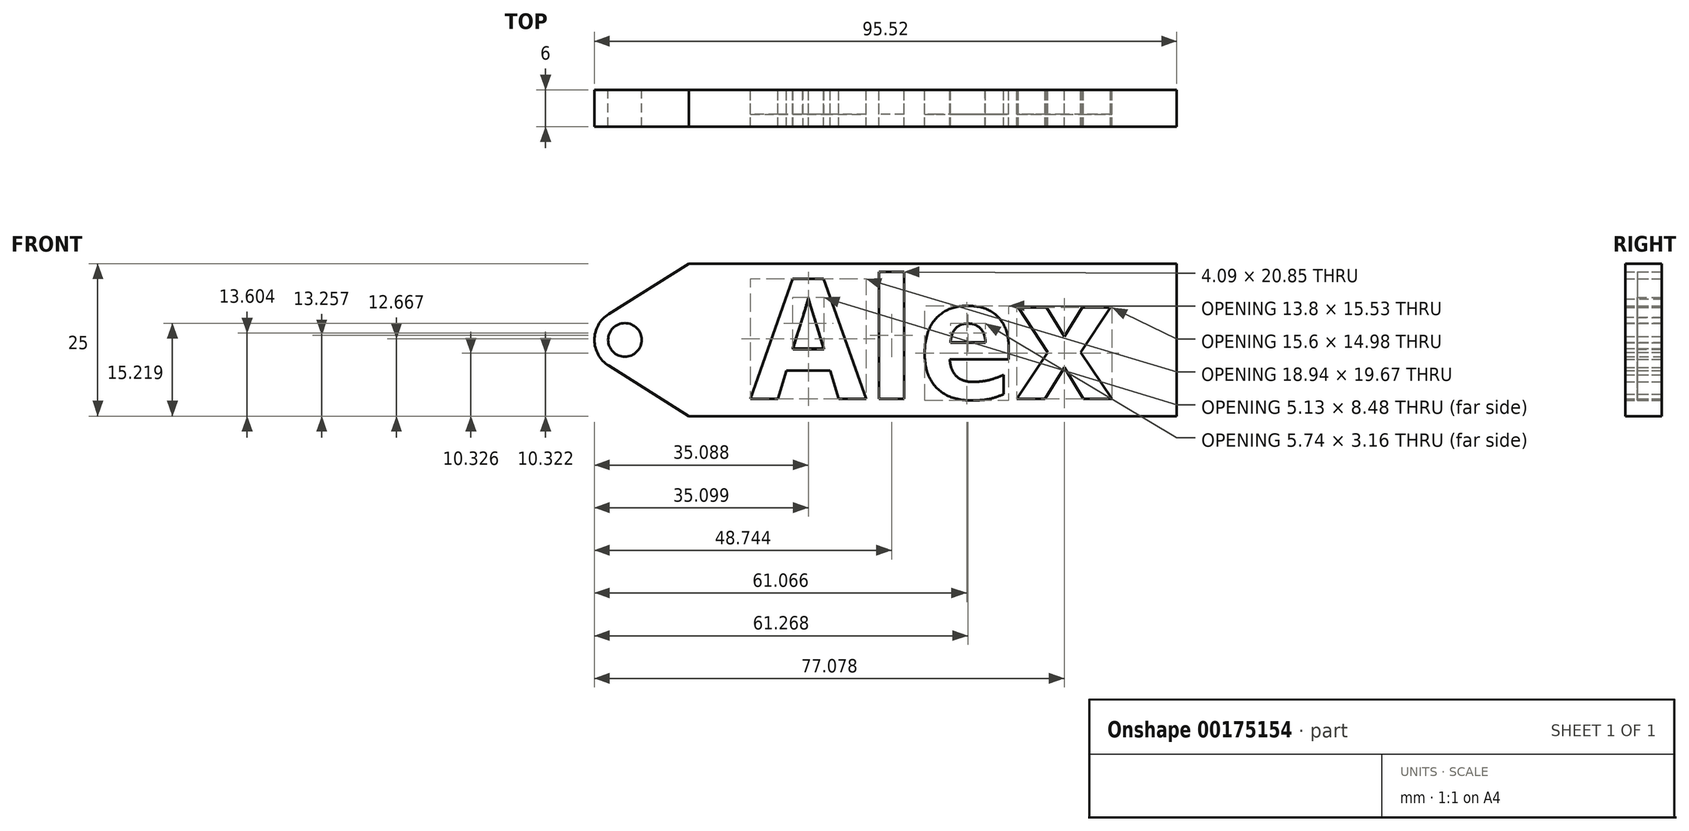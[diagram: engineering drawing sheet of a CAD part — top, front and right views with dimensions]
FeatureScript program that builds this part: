
annotation { "Feature Type Name" : "Feature", "Feature Type Description" : "" }
export const myFeature = defineFeature(function(context is Context, id is Id, definition is map)
    precondition{}
    {
        {
            var Q0;
            Q0=qCreatedBy(makeId("Front.planeOp"),FACE);
            var sketch = newSketch(context, id + "F0", { "sketchPlane" : qUnion([Q0])});
            skLineSegment(sketch, "E0.bottom", {"start": v(40, -12.5) * mm, "end": v(-40, -12.5) * mm});
            skLineSegment(sketch, "E0.top", {"start": v(40, 12.5) * mm, "end": v(-40, 12.5) * mm});
            skLineSegment(sketch, "E0.left", {"start": v(40, -12.5) * mm, "end": v(40, 12.5) * mm});
            skLineSegment(sketch, "E0.right", {"start": v(-40, -12.5) * mm, "end": v(-40, 12.5) * mm});
            skPoint(sketch, "E0.middle", {"position": v(0, 0) * mm});
            skPoint(sketch, "E1.endSnap0", {"position": v(-40, 0) * mm});
            skLineSegment(sketch, "E2", {"start": v(-53.18, 4.24) * mm, "end": v(-40, 12.5) * mm});
            skLineSegment(sketch, "E3", {"start": v(-53.18, -4.24) * mm, "end": v(-40, -12.5) * mm});
            skText(sketch, "E4", { "text": "Alex", "fontName": "OpenSans-Bold.ttf"});
            skPoint(sketch, "E5.visualSharp", {"position": v(-59.93, 0) * mm});
            skArc(sketch, "E5.filletArc", {"start": v(-53.18, 4.24) * mm, "mid": v(-55.52, 0) * mm, "end": v(-53.18, -4.24) * mm});
            skCircle(sketch, "E6", {"center": v(-50.52, 0) * mm, "radius": 2.75 * mm});
            skLineSegment(sketch, "E7", {"start": v(-22.99, -1.43) * mm, "end": v(-20.41, 6.7) * mm});
            skLineSegment(sketch, "E8", {"start": v(-20.41, 6.7) * mm, "end": v(-17.94, -1.43) * mm});
            skLineSegment(sketch, "E9", {"start": v(-22.99, -1.43) * mm, "end": v(-17.94, -1.43) * mm});
            skLineSegment(sketch, "E10", {"start": v(2.91, -0.4) * mm, "end": v(8.58, -0.4) * mm});
            skArc(sketch, "E11", {"start": v(2.91, -0.4) * mm, "mid": v(8.3, -1.36) * mm, "end": v(4.12, 2.16) * mm});
            const initialGuessF0  = {"E4": [-0.0299, -0.00967, 1, 0, 0.01976]};
            skSetInitialGuess(sketch, initialGuessF0);
            skSolve(sketch);
        }
        {
            var Q0;
            Q0=makeQuery(id+"F0.imprint","IMPRINT",FACE,{"disambiguationData":[TD([[makeQuery(id+"F0.imprint","IMPRINT",EDGE,{"derivedFrom":sQuery(id+"F0.wireOp",EDGE,"E4.sketch_text.stroke-0")}),-1.0]])]});
            var Q1;
            Q1=makeQuery(id+"F0.imprint","IMPRINT",FACE,{"disambiguationData":[TD([[makeQuery(id+"F0.imprint","IMPRINT",EDGE,{"derivedFrom":sQuery(id+"F0.wireOp",EDGE,"E4.sketch_text.stroke-12")}),-1.0]])]});
            var Q2;
            Q2=makeQuery(id+"F0.imprint","IMPRINT",FACE,{"disambiguationData":[TD([[makeQuery(id+"F0.imprint","IMPRINT",EDGE,{"derivedFrom":sQuery(id+"F0.wireOp",EDGE,"E4.sketch_text.stroke-16")}),-1.0]])]});
            var Q3;
            Q3=makeQuery(id+"F0.imprint","IMPRINT",FACE,{"disambiguationData":[TD([[makeQuery(id+"F0.imprint","IMPRINT",EDGE,{"derivedFrom":sQuery(id+"F0.wireOp",EDGE,"E4.sketch_text.stroke-36")}),-1.0]])]});
            var Q4;
            {var subQ0=sQuery(id+"F0.wireOp",EDGE,"E11");var subQ1=sQuery(id+"F0.wireOp",EDGE,"E4.sketch_text.stroke-18");var subQ2=makeQuery(id+"F0.imprint","INTERSECT",VERTEX,{"disambiguationData":[OD(0.0)],"derivedFrom":[subQ1,subQ0]});Q4=makeQuery(id+"F0.imprint","IMPRINT",FACE,{"disambiguationData":[TD([[makeQuery(id+"F0.imprint","IMPRINT",EDGE,{"disambiguationData":[TD([[subQ2,-1.0]])],"derivedFrom":subQ1}),-1.0]])]});}
            extrude(context, id + "F1", {"entities" : qUnion([Q0, Q1, Q2, Q3, Q4]), "depth" : 4 * mm});
        }
        {
            var Q0;
            Q0 = qSketchRegion(id + "F0", true);
            var Q1;
            {var subQ5=sQuery(id+"F0.wireOp",EDGE,"E8");Q1=makeQuery(id+"F0.imprint","IMPRINT",FACE,{"disambiguationData":[TD([[makeQuery(id+"F0.imprint","IMPRINT",EDGE,{"derivedFrom":subQ5}),-1.0]])]});}
            var Q2;
            Q2=makeQuery(id+"F0.imprint","IMPRINT",FACE,{"disambiguationData":[TD([[makeQuery(id+"F0.imprint","IMPRINT",EDGE,{"derivedFrom":sQuery(id+"F0.wireOp",EDGE,"E4.sketch_text.stroke-16")}),1.0]])]});
            extrude(context, id + "F2", {"entities" : qUnion([Q0, Q1, Q2]), "depth" : 6 * mm});
        }
    });
